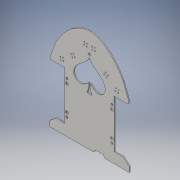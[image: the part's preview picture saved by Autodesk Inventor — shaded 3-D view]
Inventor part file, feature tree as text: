
AUTODESK INVENTOR PART (.ipt)
format: ipt  version: 2016 (Build 200138000, 138)  size: 434,688 bytes
history: native  units: mm
features: other x6, extrude x3, chamfer x1, sketch x1
ambient origin geometry x8: Origin, YZ Plane, XZ Plane, XY Plane, X Axis, Y Axis, Z Axis, Center Point
bodies: Body1 (feature_tree)
feature tree (11):
  other  "shitaita"
  other  "肉抜き"
  other  "作業平面1"
  other  "スペード"
  other  "作業平面3"
  extrude  "押し出し11"  Depth=46.0mm
  extrude  "押し出し12"  Depth=23.5mm
  extrude  "押し出し16"  Depth=23.5mm
  chamfer  "面取り1"  Distance=32.0mm
  sketch  "スケッチ20"
  other  "断面エッジを投影3"
